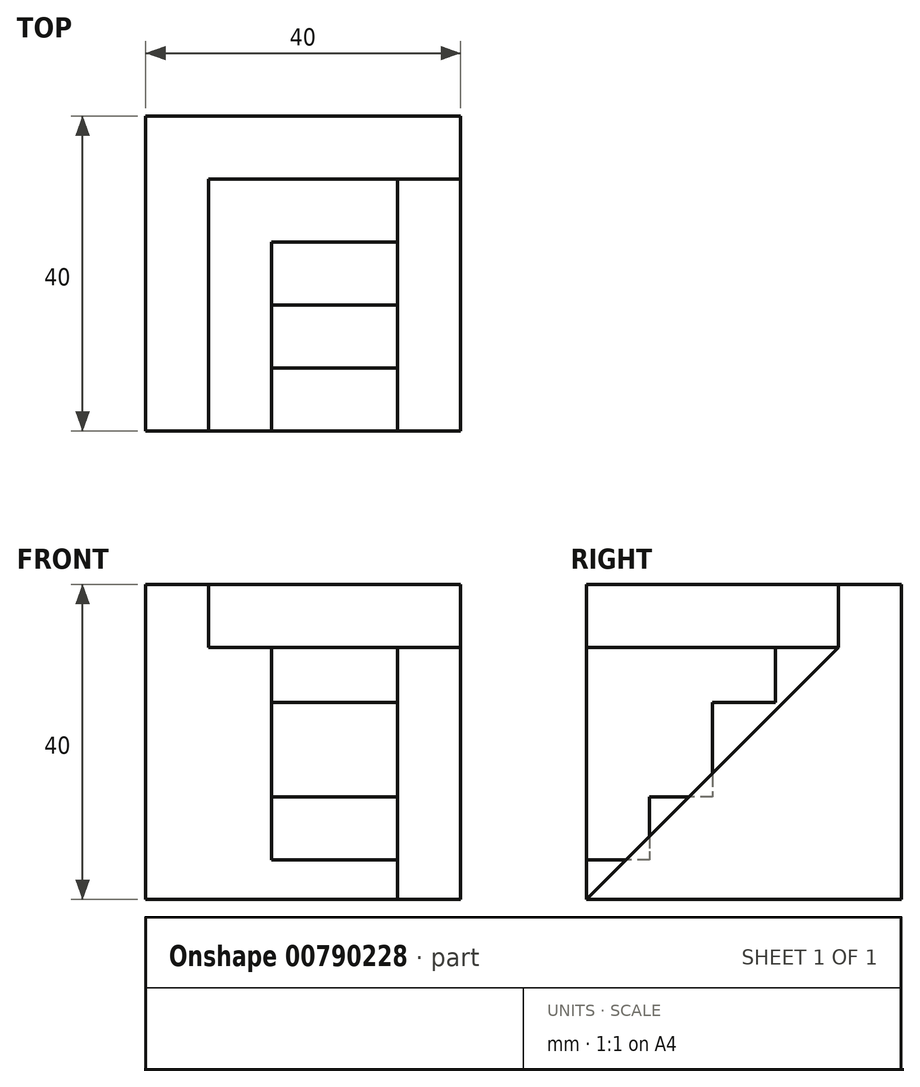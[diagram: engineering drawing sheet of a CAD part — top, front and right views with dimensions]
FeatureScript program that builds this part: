
annotation { "Feature Type Name" : "Feature", "Feature Type Description" : "" }
export const myFeature = defineFeature(function(context is Context, id is Id, definition is map)
    precondition{}
    {
        {
            var Q0;
            Q0=qCreatedBy(makeId("Top.planeOp"),FACE);
            var sketch = newSketch(context, id + "F0", { "sketchPlane" : qUnion([Q0])});
            skLineSegment(sketch, "E0.bottom", {"start": v(20, -20) * mm, "end": v(-20, -20) * mm});
            skLineSegment(sketch, "E0.top", {"start": v(20, 20) * mm, "end": v(-20, 20) * mm});
            skLineSegment(sketch, "E0.left", {"start": v(20, -20) * mm, "end": v(20, 20) * mm});
            skLineSegment(sketch, "E0.right", {"start": v(-20, -20) * mm, "end": v(-20, 20) * mm});
            skPoint(sketch, "E0.middle", {"position": v(0, 0) * mm});
            skLineSegment(sketch, "E1", {"start": v(-20, 20) * mm, "end": v(-12, 20) * mm});
            skLineSegment(sketch, "E2", {"start": v(-12, 12) * mm, "end": v(-12, -20) * mm});
            skLineSegment(sketch, "E3", {"start": v(-12, 12) * mm, "end": v(20, 12) * mm});
            skLineSegment(sketch, "E4", {"start": v(-4, 4) * mm, "end": v(-4, -20) * mm});
            skLineSegment(sketch, "E5", {"start": v(-4, 4) * mm, "end": v(12, 4) * mm});
            skLineSegment(sketch, "E6", {"start": v(-4, -4) * mm, "end": v(12, -4) * mm});
            skLineSegment(sketch, "E7", {"start": v(12, 12) * mm, "end": v(12, -20) * mm});
            skPoint(sketch, "E8.orphan", {"position": v(-20, 12) * mm});
            skPoint(sketch, "E9.orphan", {"position": v(20, 4) * mm});
            skPoint(sketch, "E10.orphan", {"position": v(20, -4) * mm});
            skPoint(sketch, "E11.orphan", {"position": v(20, -12) * mm});
            skLineSegment(sketch, "E12.trimOffspring", {"start": v(-4, -12) * mm, "end": v(12, -12) * mm});
            skPoint(sketch, "E13.start.orphan", {"position": v(-20, -12) * mm});
            skSolve(sketch);
        }
        {
            var Q0;
            {var subQ4=sQuery(id+"F0.wireOp",EDGE,"E0.left");var subQ6=sQuery(id+"F0.wireOp",EDGE,"E0.bottom");var subQ7=makeQuery(id+"F0.imprint","INTERSECT",VERTEX,{"derivedFrom":[subQ6,subQ4]});Q0=makeQuery(id+"F0.imprint","IMPRINT",FACE,{"disambiguationData":[TD([[makeQuery(id+"F0.imprint","IMPRINT",EDGE,{"disambiguationData":[TD([[subQ7,-1.0]])],"derivedFrom":subQ6}),-1.0]])]});}
            extrude(context, id + "F1", {"entities" : qUnion([Q0]), "depth" : 32 * mm, "offsetDistance" : 25 * mm});
        }
        {
            var Q0;
            Q0=makeQuery(id+"F1.opExtrude","SWEPT_FACE",FACE,{"disambiguationData":[OSD([sQuery(id+"F0.wireOp",EDGE,"E0.left")])]});
            var sketch = newSketch(context, id + "F2", { "sketchPlane" : qUnion([Q0])});
            skLineSegment(sketch, "E14", {"start": v(12, 32) * mm, "end": v(-20, 0) * mm});
            skSolve(sketch);
        }
        {
            var Q0;
            Q0=makeQuery(id+"F2.imprint","IMPRINT",FACE,{"disambiguationData":[TD([[makeQuery(id+"F2.imprint","IMPRINT",EDGE,{"derivedFrom":sQuery(id+"F2.wireOp",EDGE,"E14")}),-1.0]])]});
            extrude(context, id + "F3", {"entities" : qUnion([Q0]), "operationType" : NewBodyOperationType.REMOVE, "oppositeDirection" : true, "depth" : 25 * mm, "offsetDistance" : 25 * mm});
        }
        {
            var Q0;
            {var subQ2=sQuery(id+"F0.wireOp",EDGE,"E0.top");Q0=makeQuery(id+"F0.imprint","IMPRINT",FACE,{"disambiguationData":[TD([[makeQuery(id+"F0.imprint","IMPRINT",EDGE,{"derivedFrom":subQ2}),1.0]])]});}
            extrude(context, id + "F4", {"entities" : qUnion([Q0]), "operationType" : NewBodyOperationType.ADD, "depth" : 40 * mm, "offsetDistance" : 25 * mm});
        }
        {
            var Q0;
            {var subQ1=sQuery(id+"F0.wireOp",EDGE,"E2");Q0=makeQuery(id+"F0.imprint","IMPRINT",FACE,{"disambiguationData":[TD([[makeQuery(id+"F0.imprint","IMPRINT",EDGE,{"derivedFrom":subQ1}),1.0]])]});}
            extrude(context, id + "F5", {"entities" : qUnion([Q0]), "operationType" : NewBodyOperationType.ADD, "depth" : 32 * mm, "offsetDistance" : 25 * mm});
        }
        {
            var Q0;
            {var subQ0=sQuery(id+"F0.wireOp",EDGE,"E5");Q0=makeQuery(id+"F0.imprint","IMPRINT",FACE,{"disambiguationData":[TD([[makeQuery(id+"F0.imprint","IMPRINT",EDGE,{"derivedFrom":subQ0}),-1.0]])]});}
            extrude(context, id + "F6", {"entities" : qUnion([Q0]), "operationType" : NewBodyOperationType.ADD, "depth" : 25 * mm, "offsetDistance" : 25 * mm});
        }
        {
            var Q0;
            {var subQ0=sQuery(id+"F0.wireOp",EDGE,"E6");Q0=makeQuery(id+"F0.imprint","IMPRINT",FACE,{"disambiguationData":[TD([[makeQuery(id+"F0.imprint","IMPRINT",EDGE,{"derivedFrom":subQ0}),-1.0]])]});}
            extrude(context, id + "F7", {"entities" : qUnion([Q0]), "operationType" : NewBodyOperationType.ADD, "depth" : 13 * mm, "offsetDistance" : 25 * mm});
        }
        {
            var Q0;
            {var subQ5=sQuery(id+"F0.wireOp",EDGE,"E12.trimOffspring");Q0=makeQuery(id+"F0.imprint","IMPRINT",FACE,{"disambiguationData":[TD([[makeQuery(id+"F0.imprint","IMPRINT",EDGE,{"derivedFrom":subQ5}),-1.0]])]});}
            extrude(context, id + "F8", {"entities" : qUnion([Q0]), "operationType" : NewBodyOperationType.ADD, "depth" : 5 * mm, "offsetDistance" : 25 * mm});
        }
    });
